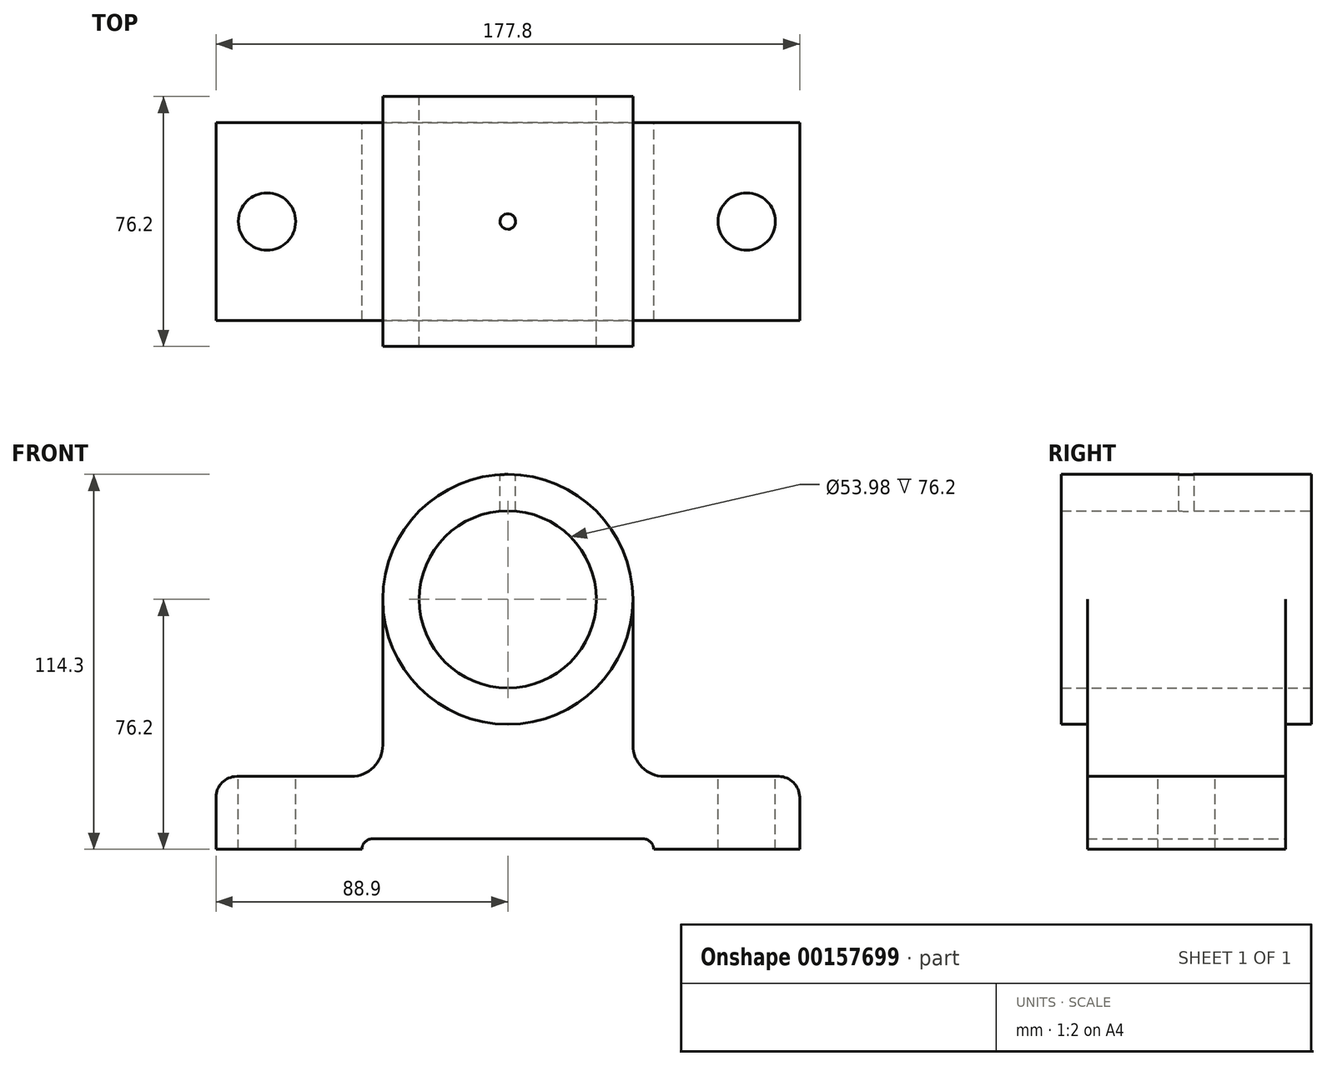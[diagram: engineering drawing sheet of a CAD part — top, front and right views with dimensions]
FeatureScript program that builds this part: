
annotation { "Feature Type Name" : "Feature", "Feature Type Description" : "" }
export const myFeature = defineFeature(function(context is Context, id is Id, definition is map)
    precondition{}
    {
        {
            var Q0;
            Q0=qCreatedBy(makeId("Front.planeOp"),FACE);
            var sketch = newSketch(context, id + "F0", { "sketchPlane" : qUnion([Q0])});
            skLineSegment(sketch, "E0", {"start": v(-88.9, 0) * mm, "end": v(-44.45, 0) * mm});
            skLineSegment(sketch, "E1", {"start": v(88.9, 0) * mm, "end": v(44.45, 0) * mm});
            skLineSegment(sketch, "E2", {"start": v(-44.45, 0) * mm, "end": v(-44.45, 0) * mm});
            skLineSegment(sketch, "E3", {"start": v(44.45, 0) * mm, "end": v(44.45, 0) * mm});
            skLineSegment(sketch, "E4", {"start": v(41.28, 3.18) * mm, "end": v(-41.28, 3.18) * mm});
            skPoint(sketch, "E5.visualSharp", {"position": v(-44.45, 3.18) * mm});
            skArc(sketch, "E5.filletArc", {"start": v(-41.28, 3.18) * mm, "mid": v(-43.52, 2.25) * mm, "end": v(-44.45, 0) * mm});
            skPoint(sketch, "E6.visualSharp", {"position": v(44.45, 3.18) * mm});
            skArc(sketch, "E6.filletArc", {"start": v(44.45, 0) * mm, "mid": v(43.52, 2.25) * mm, "end": v(41.28, 3.18) * mm});
            skLineSegment(sketch, "E7", {"start": v(-88.9, 0) * mm, "end": v(-88.9, 15.87) * mm});
            skLineSegment(sketch, "E8", {"start": v(0, 0) * mm, "end": v(-38.1, 0) * mm});
            skLineSegment(sketch, "E9", {"start": v(0, 0) * mm, "end": v(38.1, 0) * mm});
            skLineSegment(sketch, "E10", {"start": v(-82.55, 22.22) * mm, "end": v(-47.62, 22.22) * mm});
            skLineSegment(sketch, "E11", {"start": v(88.9, 0) * mm, "end": v(88.9, 15.88) * mm});
            skLineSegment(sketch, "E12", {"start": v(82.55, 22.23) * mm, "end": v(47.62, 22.23) * mm});
            skPoint(sketch, "E13.visualSharp", {"position": v(-88.9, 22.22) * mm});
            skArc(sketch, "E13.filletArc", {"start": v(-82.55, 22.22) * mm, "mid": v(-87.04, 20.37) * mm, "end": v(-88.9, 15.87) * mm});
            skPoint(sketch, "E14.visualSharp", {"position": v(88.9, 22.23) * mm});
            skArc(sketch, "E14.filletArc", {"start": v(88.9, 15.88) * mm, "mid": v(87.04, 20.37) * mm, "end": v(82.55, 22.23) * mm});
            skLineSegment(sketch, "E15", {"start": v(-38.1, 31.75) * mm, "end": v(-38.1, 76.2) * mm});
            skLineSegment(sketch, "E16", {"start": v(38.1, 31.75) * mm, "end": v(38.1, 76.2) * mm});
            skPoint(sketch, "E17.newPointB", {"position": v(-38.1, 0) * mm});
            skArc(sketch, "E17.filletArc", {"start": v(-47.62, 22.23) * mm, "mid": v(-40.89, 25.01) * mm, "end": v(-38.1, 31.75) * mm});
            skPoint(sketch, "E18.newPointB", {"position": v(38.1, 0) * mm});
            skArc(sketch, "E18.filletArc", {"start": v(38.1, 31.75) * mm, "mid": v(40.89, 25.01) * mm, "end": v(47.62, 22.23) * mm});
            skCircle(sketch, "E19", {"center": v(0, 76.2) * mm, "radius": 38.1 * mm});
            skCircle(sketch, "E20", {"center": v(0, 76.2) * mm, "radius": 20.64 * mm});
            skCircle(sketch, "E21", {"center": v(0, 76.2) * mm, "radius": 26.99 * mm});
            skSolve(sketch);
        }
        {
            var Q0;
            Q0=makeQuery(id+"F0.imprint","IMPRINT",FACE,{"disambiguationData":[TD([[makeQuery(id+"F0.imprint","IMPRINT",EDGE,{"derivedFrom":sQuery(id+"F0.wireOp",EDGE,"E0")}),1.0]])]});
            extrude(context, id + "F1", {"entities" : qUnion([Q0]), "endBound" : BoundingType.SYMMETRIC, "depth" : 60.32 * mm});
        }
        {
            var Q0;
            Q0=makeQuery(id+"F0.imprint","IMPRINT",FACE,{"disambiguationData":[TD([[makeQuery(id+"F0.imprint","IMPRINT",EDGE,{"derivedFrom":sQuery(id+"F0.wireOp",EDGE,"E21")}),-1.0]])]});
            extrude(context, id + "F2", {"entities" : qUnion([Q0]), "operationType" : NewBodyOperationType.ADD, "endBound" : BoundingType.SYMMETRIC, "depth" : 76.2 * mm});
        }
        {
            var Q0;
            Q0=makeQuery(id+"F1.opExtrude","SWEPT_FACE",FACE,{"disambiguationData":[OSD([sQuery(id+"F0.wireOp",EDGE,"E12")])]});
            var sketch = newSketch(context, id + "F3", { "sketchPlane" : qUnion([Q0])});
            skCircle(sketch, "E22", {"center": v(72.78, 0) * mm, "radius": 8.73 * mm});
            skSolve(sketch);
        }
        {
            var Q0;
            Q0 = qSketchRegion(id + "F3", true);
            extrude(context, id + "F4", {"entities" : qUnion([Q0]), "operationType" : NewBodyOperationType.REMOVE, "oppositeDirection" : true, "depth" : 25.4 * mm});
        }
        {
            var Q0;
            Q0=makeQuery(id+"F1.opExtrude","SWEPT_FACE",FACE,{"disambiguationData":[OSD([sQuery(id+"F0.wireOp",EDGE,"E10")])]});
            var sketch = newSketch(context, id + "F5", { "sketchPlane" : qUnion([Q0])});
            skCircle(sketch, "E23", {"center": v(-73.33, 0) * mm, "radius": 8.73 * mm});
            skSolve(sketch);
        }
        {
            var Q0;
            Q0 = qSketchRegion(id + "F5", true);
            extrude(context, id + "F6", {"entities" : qUnion([Q0]), "operationType" : NewBodyOperationType.REMOVE, "oppositeDirection" : true, "depth" : 25.4 * mm});
        }
        {
            var Q0;
            Q0=qCreatedBy(makeId("Top.planeOp"),FACE);
            cPlane(context, id + "F7", {"entities" : qUnion([Q0]), "cplaneType" : CPlaneType.OFFSET, "offset" : 114.3 * mm, "width" : 152.4 * mm, "height" : 152.4 * mm});
        }
        {
            var Q0;
            Q0=qCreatedBy(id+"F7.planeOp",FACE);
            var sketch = newSketch(context, id + "F8", { "sketchPlane" : qUnion([Q0])});
            skCircle(sketch, "E24", {"center": v(0, 0) * mm, "radius": 2.38 * mm});
            skSolve(sketch);
        }
        {
            var Q0;
            Q0 = qSketchRegion(id + "F8", true);
            extrude(context, id + "F9", {"entities" : qUnion([Q0]), "operationType" : NewBodyOperationType.REMOVE, "oppositeDirection" : true, "depth" : 25.4 * mm});
        }
    });
